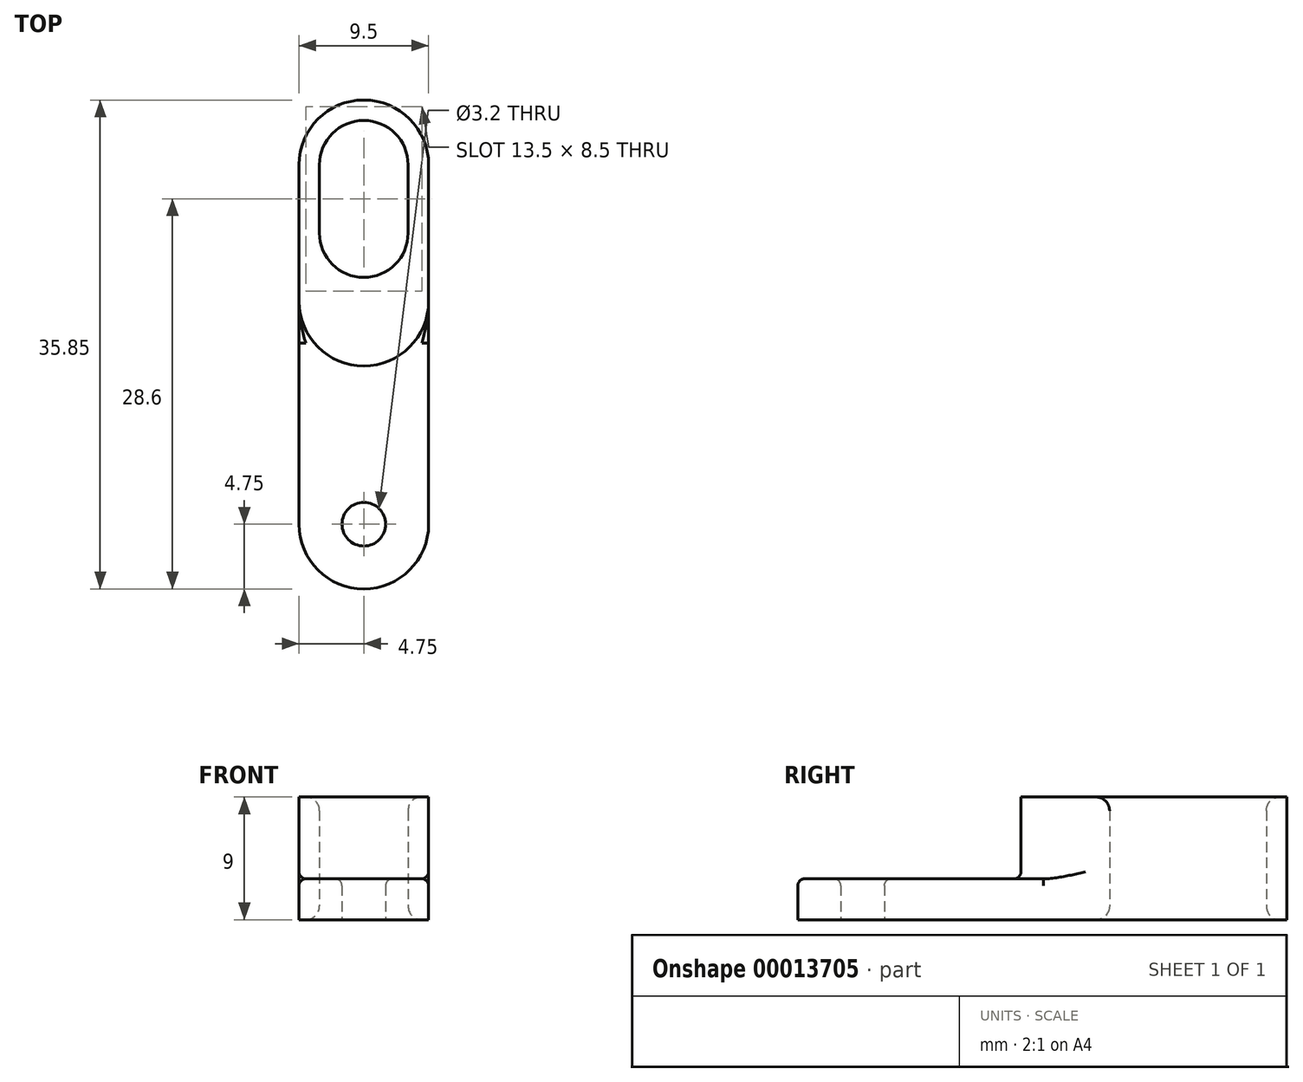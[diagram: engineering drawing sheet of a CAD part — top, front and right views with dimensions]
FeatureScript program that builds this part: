
annotation { "Feature Type Name" : "Feature", "Feature Type Description" : "" }
export const myFeature = defineFeature(function(context is Context, id is Id, definition is map)
    precondition{}
    {
        {
            var Q0;
            Q0=qCreatedBy(makeId("Top.planeOp"),FACE);
            var sketch = newSketch(context, id + "F0", { "sketchPlane" : qUnion([Q0])});
            skArc(sketch, "E0", {"start": v(-3.25, 0) * mm, "mid": v(0, -3.25) * mm, "end": v(3.25, 0) * mm});
            skArc(sketch, "E1", {"start": v(-4.75, 0) * mm, "mid": v(0, -4.75) * mm, "end": v(4.75, 0) * mm});
            skArc(sketch, "E2", {"start": v(3.25, 10) * mm, "mid": v(0, 13.25) * mm, "end": v(-3.25, 10) * mm});
            skArc(sketch, "E3", {"start": v(4.75, 10) * mm, "mid": v(0, 14.75) * mm, "end": v(-4.75, 10) * mm});
            skLineSegment(sketch, "E4", {"start": v(3.25, 10) * mm, "end": v(3.25, 0) * mm});
            skLineSegment(sketch, "E5", {"start": v(-3.25, 10) * mm, "end": v(-3.25, 0) * mm});
            skLineSegment(sketch, "E6", {"start": v(4.75, 10) * mm, "end": v(4.75, 0) * mm});
            skLineSegment(sketch, "E7", {"start": v(-4.75, 10) * mm, "end": v(-4.75, 0) * mm});
            skCircle(sketch, "E8", {"center": v(0, -16.35) * mm, "radius": 1.6 * mm});
            skArc(sketch, "E9", {"start": v(-4.75, -16.35) * mm, "mid": v(0, -21.1) * mm, "end": v(4.75, -16.35) * mm});
            skLineSegment(sketch, "E10", {"start": v(4.75, -16.35) * mm, "end": v(4.75, 0) * mm});
            skLineSegment(sketch, "E11", {"start": v(-4.75, -16.35) * mm, "end": v(-4.75, 0) * mm});
            skArc(sketch, "E12", {"start": v(-3.25, 5) * mm, "mid": v(0, 1.75) * mm, "end": v(3.25, 5) * mm});
            skSolve(sketch);
        }
        {
            var Q0;
            Q0=makeQuery(id+"F0.imprint","IMPRINT",FACE,{"disambiguationData":[TD([[makeQuery(id+"F0.imprint","IMPRINT",EDGE,{"derivedFrom":sQuery(id+"F0.wireOp",EDGE,"E1")}),-1.0]])]});
            var Q1;
            {var subQ6=sQuery(id+"F0.wireOp",EDGE,"E0");Q1=makeQuery(id+"F0.imprint","IMPRINT",FACE,{"disambiguationData":[TD([[makeQuery(id+"F0.imprint","IMPRINT",EDGE,{"derivedFrom":subQ6}),-1.0]])]});}
            extrude(context, id + "F1", {"entities" : qUnion([Q0, Q1]), "depth" : 3 * mm});
        }
        {
            var Q0;
            {var subQ6=sQuery(id+"F0.wireOp",EDGE,"E0");Q0=makeQuery(id+"F0.imprint","IMPRINT",FACE,{"disambiguationData":[TD([[makeQuery(id+"F0.imprint","IMPRINT",EDGE,{"derivedFrom":subQ6}),-1.0]])]});}
            var Q1;
            {var subQ2=sQuery(id+"F0.wireOp",EDGE,"E0");Q1=makeQuery(id+"F0.imprint","IMPRINT",FACE,{"disambiguationData":[TD([[makeQuery(id+"F0.imprint","IMPRINT",EDGE,{"derivedFrom":subQ2}),1.0]])]});}
            extrude(context, id + "F2", {"entities" : qUnion([Q0, Q1]), "operationType" : NewBodyOperationType.ADD, "depth" : 9 * mm});
        }
        {
            var Q0;
            Q0=makeQuery(id+"F2.opExtrude","CAP_EDGE",EDGE,{"disambiguationData":[OSD([sQuery(id+"F0.wireOp",EDGE,"E12")])],"isStart":false});
            var Q1;
            Q1=makeQuery(id+"F2.opExtrude","CAP_EDGE",EDGE,{"disambiguationData":[OSD([sQuery(id+"F0.wireOp",EDGE,"E12")])],"isStart":true});
            fillet(context, id + "F3", {"entities" : qUnion([Q0, Q1]), "radius" : 1 * mm, "tangentPropagation" : true, "allowEdgeOverflow" : false});
        }
        {
            var Q0;
            Q0=makeQuery(id+"F1.opExtrude","CAP_FACE",FACE,{"disambiguationData":[OSD([sQuery(id+"F0.wireOp",EDGE,"E0"),sQuery(id+"F0.wireOp",EDGE,"E2"),sQuery(id+"F0.wireOp",EDGE,"E3"),sQuery(id+"F0.wireOp",EDGE,"E4"),sQuery(id+"F0.wireOp",EDGE,"E5"),sQuery(id+"F0.wireOp",EDGE,"E6"),sQuery(id+"F0.wireOp",EDGE,"E7"),sQuery(id+"F0.wireOp",EDGE,"E8"),sQuery(id+"F0.wireOp",EDGE,"E9"),sQuery(id+"F0.wireOp",EDGE,"E10"),sQuery(id+"F0.wireOp",EDGE,"E11")])],"isStart":false});
            fillet(context, id + "F4", {"entities" : qUnion([Q0]), "radius" : 0.5 * mm, "tangentPropagation" : true, "allowEdgeOverflow" : false});
        }
    });
